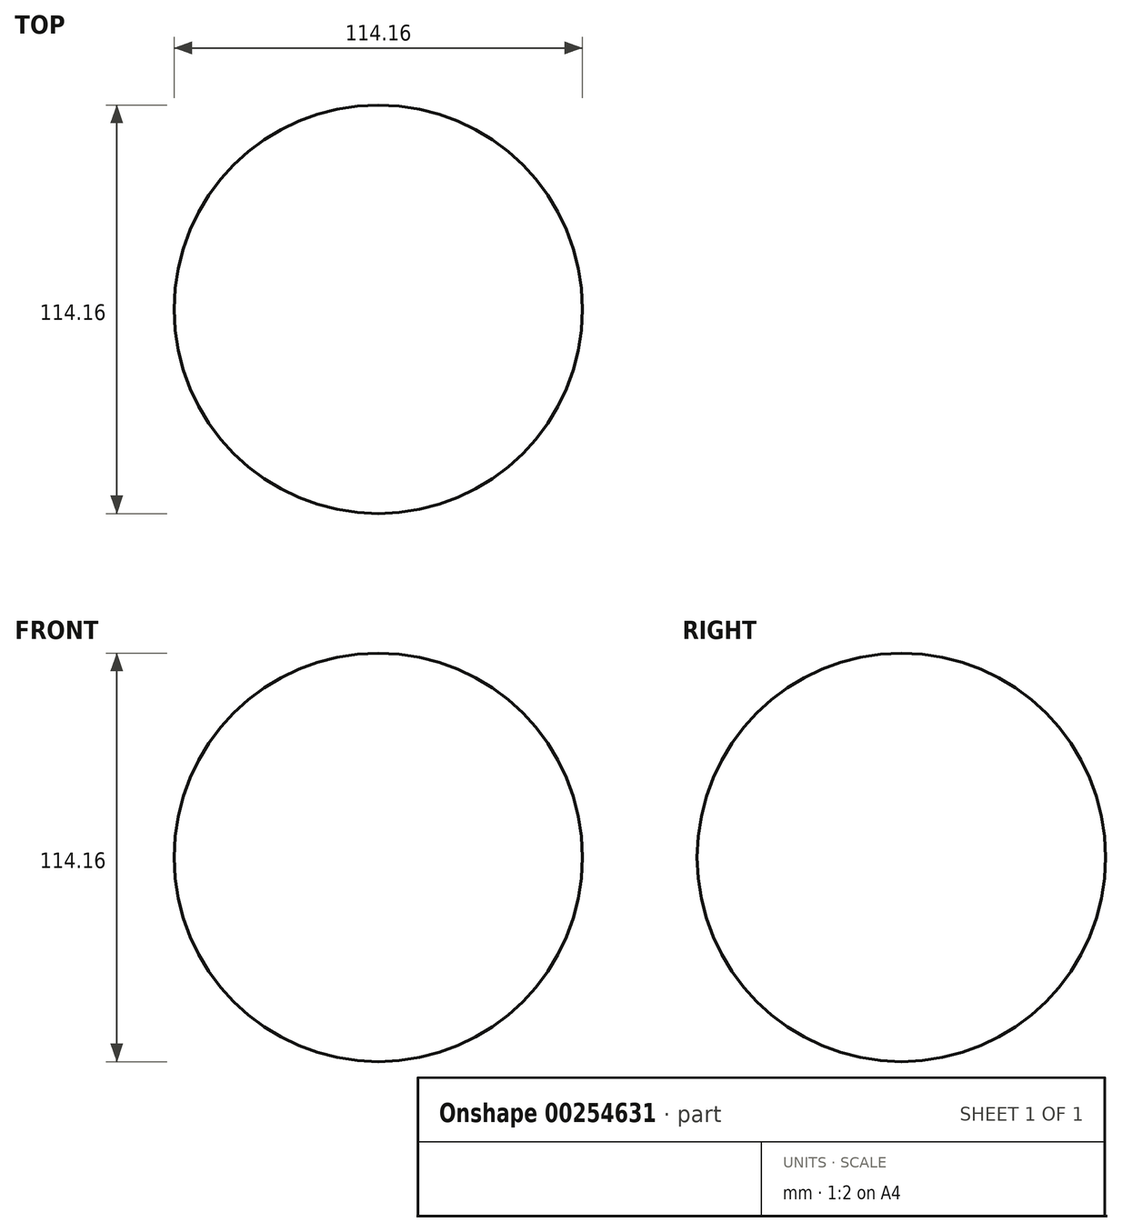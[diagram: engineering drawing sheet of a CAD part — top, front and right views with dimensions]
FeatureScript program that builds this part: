
annotation { "Feature Type Name" : "Feature", "Feature Type Description" : "" }
export const myFeature = defineFeature(function(context is Context, id is Id, definition is map)
    precondition{}
    {
        {
            var Q0;
            Q0=qCreatedBy(makeId("Front.planeOp"),FACE);
            var sketch = newSketch(context, id + "F0", { "sketchPlane" : qUnion([Q0])});
            skLineSegment(sketch, "E0", {"start": v(0, 90.48) * mm, "end": v(0, -90.4) * mm, "construction": true});
            skArc(sketch, "E1", {"start": v(0, 57.08) * mm, "mid": v(-57.08, 0) * mm, "end": v(0, -57.08) * mm});
            skSolve(sketch);
        }
        {
            var Q0;
            Q0=sQuery(id+"F0.wireOp",EDGE,"E1");
            var Q1;
            Q1=sQuery(id+"F0.wireOp",EDGE,"E0");
            revolve(context, id + "F1", {"bodyType" : ToolBodyType.SURFACE, "surfaceEntities" : qUnion([Q0]), "axis" : qUnion([Q1]), "revolveType" : RevolveType.FULL});
        }
    });
